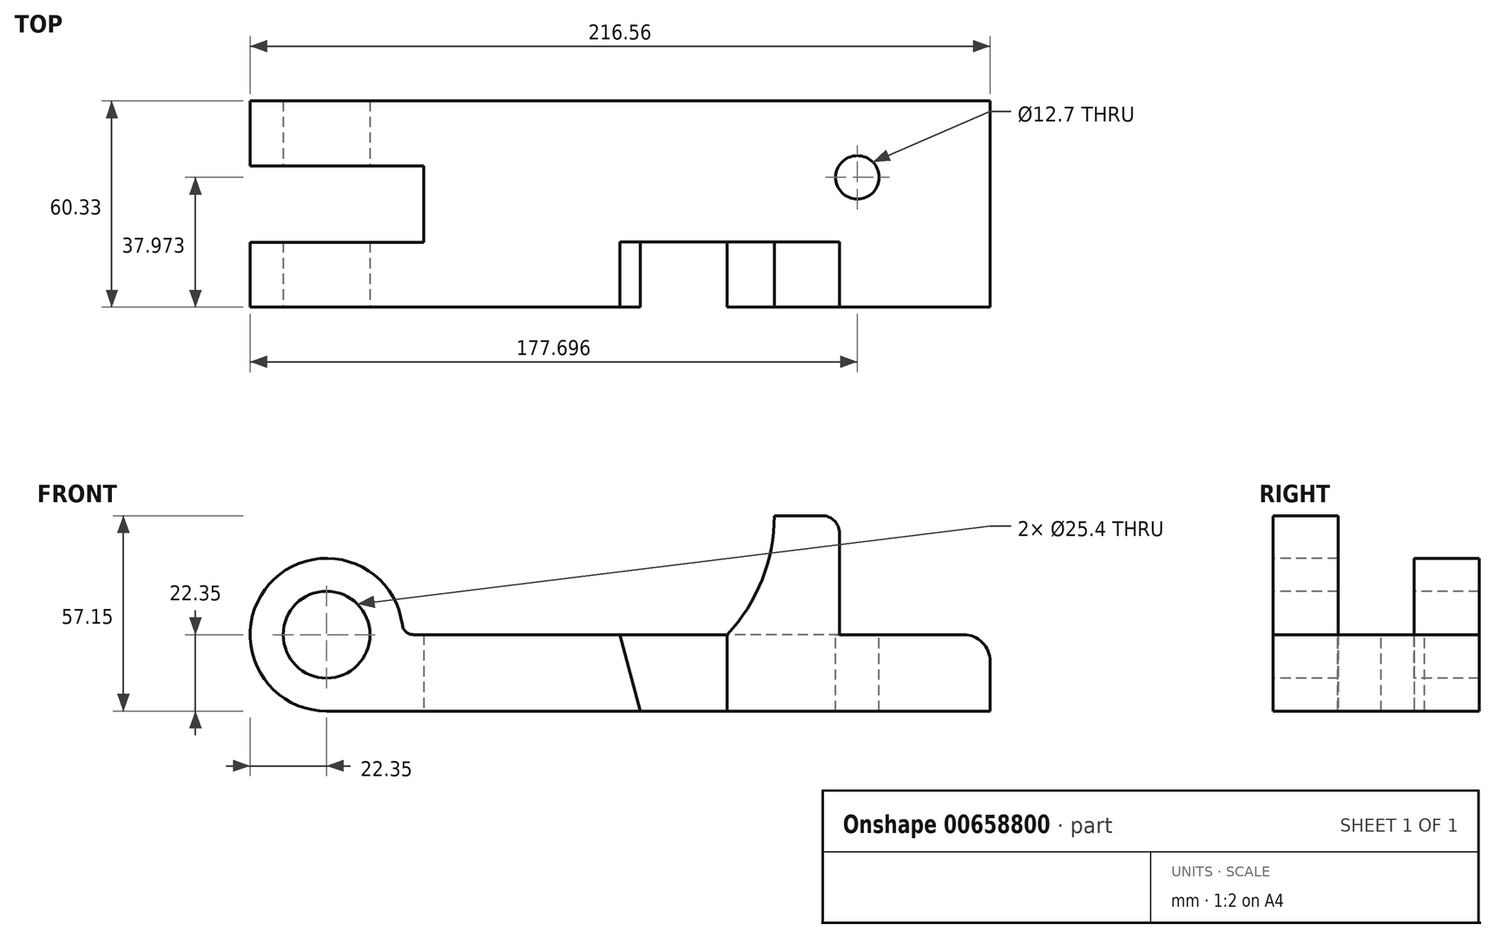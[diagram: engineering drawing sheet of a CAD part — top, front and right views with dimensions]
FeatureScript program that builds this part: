
annotation { "Feature Type Name" : "Feature", "Feature Type Description" : "" }
export const myFeature = defineFeature(function(context is Context, id is Id, definition is map)
    precondition{}
    {
        {
            var Q0;
            Q0=qCreatedBy(makeId("Front.planeOp"),FACE);
            var sketch = newSketch(context, id + "F0", { "sketchPlane" : qUnion([Q0])});
            skCircle(sketch, "E0", {"center": v(0, 0) * mm, "radius": 22.35 * mm});
            skLineSegment(sketch, "E1", {"start": v(0, -22.35) * mm, "end": v(194.2, -22.35) * mm});
            skLineSegment(sketch, "E2", {"start": v(194.2, -22.35) * mm, "end": v(194.2, 0) * mm});
            skLineSegment(sketch, "E3", {"start": v(194.2, 0) * mm, "end": v(22.35, 0) * mm});
            skCircle(sketch, "E4", {"center": v(0, 0) * mm, "radius": 12.7 * mm});
            skSolve(sketch);
        }
        {
            var Q0;
            {var subQ0=sQuery(id+"F0.wireOp",EDGE,"E1");Q0=makeQuery(id+"F0.imprint","IMPRINT",FACE,{"disambiguationData":[TD([[makeQuery(id+"F0.imprint","IMPRINT",EDGE,{"derivedFrom":subQ0}),1.0]])]});}
            var Q1;
            {var subQ0=sQuery(id+"F0.wireOp",EDGE,"E0");var subQ1=makeQuery(id+"F0.imprint","INTERSECT",VERTEX,{"derivedFrom":[subQ0,sQuery(id+"F0.wireOp",EDGE,"E1")]});Q1=makeQuery(id+"F0.imprint","IMPRINT",FACE,{"disambiguationData":[TD([[makeQuery(id+"F0.imprint","IMPRINT",EDGE,{"disambiguationData":[TD([[subQ1,1.0]])],"derivedFrom":subQ0}),1.0]])]});}
            extrude(context, id + "F1", {"entities" : qUnion([Q0, Q1]), "oppositeDirection" : true, "depth" : 60.32 * mm});
        }
        {
            var Q0;
            Q0=makeQuery(id+"F1.opExtrude","SWEPT_EDGE",EDGE,{"disambiguationData":[OSD([sQuery(id+"F0.wireOp",EDGE,"E2"),sQuery(id+"F0.wireOp",EDGE,"E3")])]});
            fillet(context, id + "F2", {"entities" : qUnion([Q0]), "radius" : 7.87 * mm, "tangentPropagation" : true, "allowEdgeOverflow" : false});
        }
        {
            var Q0;
            {var subQ0=sQuery(id+"F0.wireOp",EDGE,"E1");Q0=makeQuery(id+"F0.imprint","IMPRINT",FACE,{"disambiguationData":[TD([[makeQuery(id+"F0.imprint","IMPRINT",EDGE,{"derivedFrom":subQ0}),1.0]])]});}
            var sketch = newSketch(context, id + "F3", { "sketchPlane" : qUnion([Q0])});
            skLineSegment(sketch, "E5", {"start": v(117.25, 0) * mm, "end": v(150.09, 0) * mm});
            skLineSegment(sketch, "E6", {"start": v(150.09, 0) * mm, "end": v(150.09, 34.8) * mm});
            skLineSegment(sketch, "E7", {"start": v(150.09, 34.8) * mm, "end": v(131.04, 34.8) * mm});
            skArc(sketch, "E8", {"start": v(117.25, 0) * mm, "mid": v(127.46, 16.08) * mm, "end": v(131.04, 34.8) * mm});
            skLineSegment(sketch, "E9", {"start": v(117.25, 0) * mm, "end": v(117.25, -15.1) * mm, "construction": true});
            skSolve(sketch);
        }
        {
            var Q0;
            Q0=qSketchRegion(id+"F3",true);
            extrude(context, id + "F4", {"entities" : qUnion([Q0]), "operationType" : NewBodyOperationType.ADD, "oppositeDirection" : true, "depth" : 19.05 * mm});
        }
        {
            var Q0;
            Q0=makeQuery(id+"F4.boolean.opBoolean","MERGE",FACE,{"derivedFrom":[makeQuery(id+"F1.opExtrude","CAP_FACE",FACE,{"disambiguationData":[OSD([sQuery(id+"F0.wireOp",EDGE,"E0"),sQuery(id+"F0.wireOp",EDGE,"E1"),sQuery(id+"F0.wireOp",EDGE,"E2"),sQuery(id+"F0.wireOp",EDGE,"E3"),sQuery(id+"F0.wireOp",EDGE,"E4")])],"isStart":true}),makeQuery(id+"F4.opExtrude","CAP_FACE",FACE,{"disambiguationData":[OSD([sQuery(id+"F3.wireOp",EDGE,"E5"),sQuery(id+"F3.wireOp",EDGE,"E6"),sQuery(id+"F3.wireOp",EDGE,"E7"),sQuery(id+"F3.wireOp",EDGE,"E8")])],"isStart":true})]});
            var sketch = newSketch(context, id + "F5", { "sketchPlane" : qUnion([Q0])});
            skLineSegment(sketch, "E10", {"start": v(117.25, 0) * mm, "end": v(85.85, 0) * mm});
            skLineSegment(sketch, "E11", {"start": v(85.85, 0) * mm, "end": v(91.85, -22.35) * mm});
            skLineSegment(sketch, "E12", {"start": v(91.85, -22.35) * mm, "end": v(117.25, -22.35) * mm});
            skLineSegment(sketch, "E13", {"start": v(117.25, -22.35) * mm, "end": v(117.25, 0) * mm});
            skSolve(sketch);
        }
        {
            var Q0;
            Q0=qSketchRegion(id+"F5",true);
            extrude(context, id + "F6", {"entities" : qUnion([Q0]), "operationType" : NewBodyOperationType.REMOVE, "oppositeDirection" : true, "depth" : 19.05 * mm});
        }
        {
            var Q0;
            Q0=makeQuery(id+"F4.opExtrude","SWEPT_EDGE",EDGE,{"disambiguationData":[OSD([sQuery(id+"F3.wireOp",EDGE,"E6"),sQuery(id+"F3.wireOp",EDGE,"E7")])]});
            fillet(context, id + "F7", {"entities" : qUnion([Q0]), "radius" : 5.08 * mm, "tangentPropagation" : true, "allowEdgeOverflow" : false});
        }
        {
            var Q0;
            Q0=makeQuery(id+"F1.opExtrude","SWEPT_FACE",FACE,{"disambiguationData":[OSD([sQuery(id+"F0.wireOp",EDGE,"E3")])]});
            var sketch = newSketch(context, id + "F8", { "sketchPlane" : qUnion([Q0])});
            skCircle(sketch, "E14", {"center": v(155.35, 37.97) * mm, "radius": 6.35 * mm});
            skSolve(sketch);
        }
        {
            var Q0;
            Q0=qSketchRegion(id+"F8",true);
            extrude(context, id + "F9", {"entities" : qUnion([Q0]), "operationType" : NewBodyOperationType.REMOVE, "endBound" : BoundingType.THROUGH_ALL, "oppositeDirection" : true, "depth" : 25.4 * mm});
        }
        {
            var Q0;
            Q0=makeQuery(id+"F1.opExtrude","SWEPT_FACE",FACE,{"disambiguationData":[OSD([sQuery(id+"F0.wireOp",EDGE,"E1")])]});
            var sketch = newSketch(context, id + "F10", { "sketchPlane" : qUnion([Q0])});
            skLineSegment(sketch, "E15", {"start": v(-22.35, -41.33) * mm, "end": v(-22.35, -19) * mm});
            skLineSegment(sketch, "E16", {"start": v(-22.35, -19) * mm, "end": v(28.45, -19) * mm});
            skLineSegment(sketch, "E17", {"start": v(28.45, -19) * mm, "end": v(28.45, -41.33) * mm});
            skLineSegment(sketch, "E18", {"start": v(28.45, -41.33) * mm, "end": v(-22.35, -41.33) * mm});
            skSolve(sketch);
        }
        {
            var Q0;
            Q0=qSketchRegion(id+"F10",true);
            extrude(context, id + "F11", {"entities" : qUnion([Q0]), "operationType" : NewBodyOperationType.REMOVE, "oppositeDirection" : true, "depth" : 44.7 * mm});
        }
        {
            var Q0;
            {var subQ0=sQuery(id+"F0.wireOp",EDGE,"E3");var subQ1=sQuery(id+"F0.wireOp",EDGE,"E0");Q0=makeQuery(id+"F11.boolean.opBoolean","SPLIT",EDGE,{"disambiguationData":[TD([makeQuery(id+"F1.opExtrude","SWEPT_FACE",FACE,{"disambiguationData":[OSD([subQ1])]}),makeQuery(id+"F1.opExtrude","CAP_FACE",FACE,{"disambiguationData":[OSD([subQ1,sQuery(id+"F0.wireOp",EDGE,"E1"),sQuery(id+"F0.wireOp",EDGE,"E2"),subQ0,sQuery(id+"F0.wireOp",EDGE,"E4")])],"isStart":true}),makeQuery(id+"F1.opExtrude","SWEPT_FACE",FACE,{"disambiguationData":[OSD([subQ0])]}),makeQuery(id+"F4.opExtrude","CAP_FACE",FACE,{"disambiguationData":[OSD([sQuery(id+"F3.wireOp",EDGE,"E5"),sQuery(id+"F3.wireOp",EDGE,"E6"),sQuery(id+"F3.wireOp",EDGE,"E7"),sQuery(id+"F3.wireOp",EDGE,"E8")])],"isStart":true}),makeQuery(id+"F11.opExtrude","SWEPT_FACE",FACE,{"disambiguationData":[OSD([sQuery(id+"F10.wireOp",EDGE,"E16")])]}),makeQuery(id+"F11.opExtrude","SWEPT_FACE",FACE,{"disambiguationData":[OSD([sQuery(id+"F10.wireOp",EDGE,"E17")])]})])],"derivedFrom":makeQuery(id+"F1.opExtrude","SWEPT_EDGE",EDGE,{"disambiguationData":[OSD([subQ1,subQ0])]})});}
            var Q1;
            {var subQ0=sQuery(id+"F0.wireOp",EDGE,"E3");var subQ1=sQuery(id+"F0.wireOp",EDGE,"E0");Q1=makeQuery(id+"F11.boolean.opBoolean","SPLIT",EDGE,{"disambiguationData":[TD([makeQuery(id+"F1.opExtrude","SWEPT_FACE",FACE,{"disambiguationData":[OSD([subQ1])]}),makeQuery(id+"F1.opExtrude","CAP_FACE",FACE,{"disambiguationData":[OSD([subQ1,sQuery(id+"F0.wireOp",EDGE,"E1"),sQuery(id+"F0.wireOp",EDGE,"E2"),subQ0,sQuery(id+"F0.wireOp",EDGE,"E4")])],"isStart":false}),makeQuery(id+"F1.opExtrude","SWEPT_FACE",FACE,{"disambiguationData":[OSD([subQ0])]}),makeQuery(id+"F11.opExtrude","SWEPT_FACE",FACE,{"disambiguationData":[OSD([sQuery(id+"F10.wireOp",EDGE,"E17")])]}),makeQuery(id+"F11.opExtrude","SWEPT_FACE",FACE,{"disambiguationData":[OSD([sQuery(id+"F10.wireOp",EDGE,"E18")])]})])],"derivedFrom":makeQuery(id+"F1.opExtrude","SWEPT_EDGE",EDGE,{"disambiguationData":[OSD([subQ1,subQ0])]})});}
            var Q2;
            Q2=makeQuery(id+"F4.opExtrude","SWEPT_EDGE",EDGE,{"disambiguationData":[OSD([sQuery(id+"F0.wireOp",EDGE,"E3"),sQuery(id+"F3.wireOp",EDGE,"E5"),sQuery(id+"F3.wireOp",EDGE,"E6")])]});
            fillet(context, id + "F12", {"entities" : qUnion([Q0, Q1, Q2]), "radius" : 3.3 * mm, "tangentPropagation" : true, "allowEdgeOverflow" : false});
        }
    });
